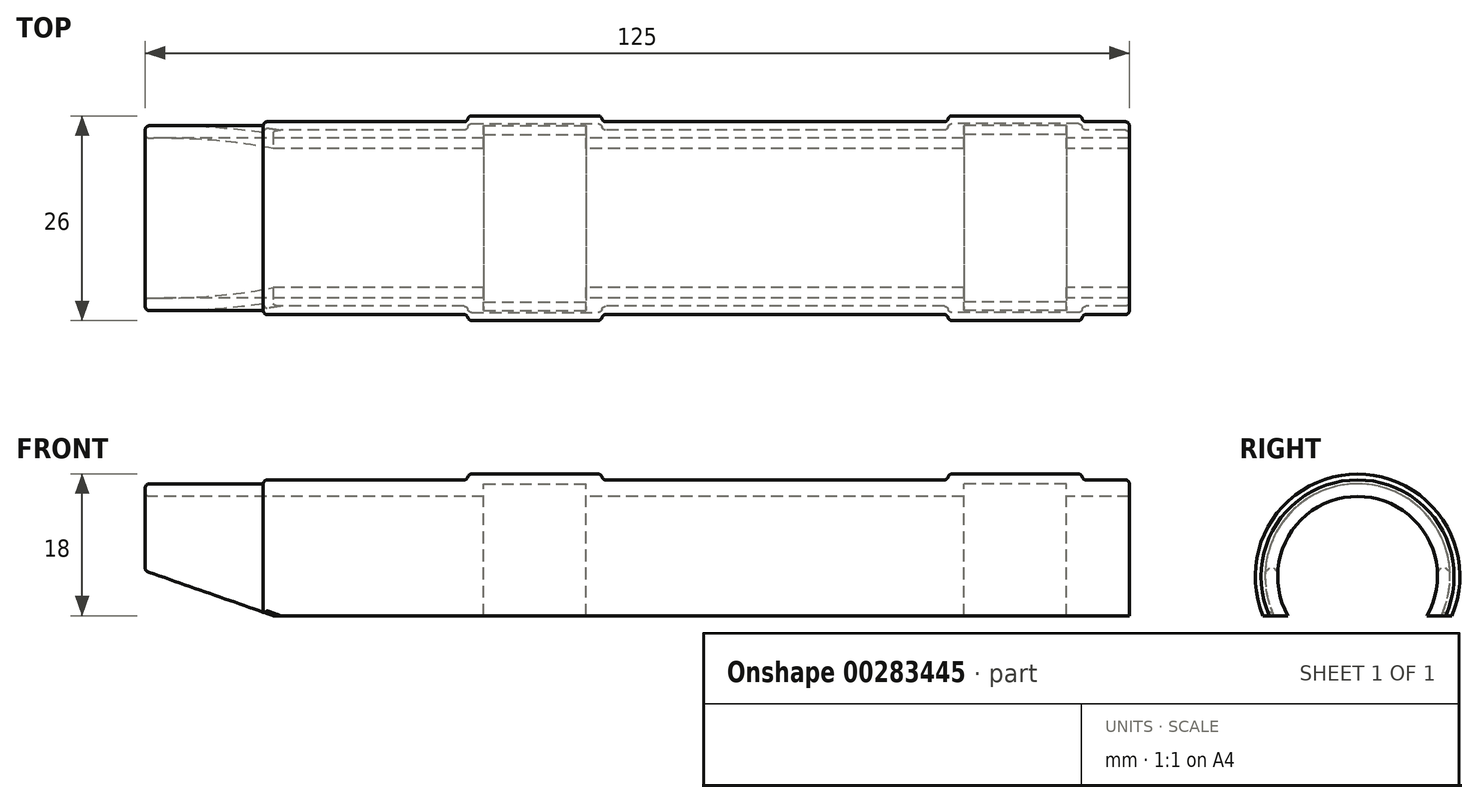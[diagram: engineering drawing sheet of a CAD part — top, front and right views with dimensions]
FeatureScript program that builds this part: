
annotation { "Feature Type Name" : "Feature", "Feature Type Description" : "" }
export const myFeature = defineFeature(function(context is Context, id is Id, definition is map)
    precondition{}
    {
        {
            var Q0;
            Q0=qCreatedBy(makeId("Right.planeOp"),FACE);
            var sketch = newSketch(context, id + "F0", { "sketchPlane" : qUnion([Q0])});
            skCircle(sketch, "E0", {"center": v(0, 0) * mm, "radius": 10.15 * mm});
            skCircle(sketch, "E1", {"center": v(0, 0) * mm, "radius": 11.75 * mm});
            skCircle(sketch, "E2", {"center": v(0, 0) * mm, "radius": 12.25 * mm});
            skLineSegment(sketch, "E3", {"start": v(0, 0) * mm, "end": v(15.86, -16.54) * mm});
            skLineSegment(sketch, "E4", {"start": v(0, 0) * mm, "end": v(-17.88, -17.15) * mm});
            skCircle(sketch, "E5", {"center": v(0, 0) * mm, "radius": 13 * mm});
            skSolve(sketch);
        }
        {
            var Q0;
            {var subQ0=sQuery(id+"F0.wireOp",EDGE,"E3");var subQ1=sQuery(id+"F0.wireOp",EDGE,"E0");var subQ2=makeQuery(id+"F0.imprint","INTERSECT",VERTEX,{"derivedFrom":[subQ1,subQ0]});Q0=makeQuery(id+"F0.imprint","IMPRINT",FACE,{"disambiguationData":[TD([[makeQuery(id+"F0.imprint","IMPRINT",EDGE,{"disambiguationData":[TD([[subQ2,-1.0]])],"derivedFrom":subQ1}),-1.0]])]});}
            extrude(context, id + "F1", {"entities" : qUnion([Q0]), "depth" : 55 * mm, "hasSecondDirection" : true, "secondDirectionOppositeDirection" : true, "secondDirectionDepth" : 70 * mm});
        }
        {
            var Q0;
            {var subQ0=sQuery(id+"F0.wireOp",EDGE,"E3");var subQ1=sQuery(id+"F0.wireOp",EDGE,"E1");var subQ2=makeQuery(id+"F0.imprint","INTERSECT",VERTEX,{"derivedFrom":[subQ1,subQ0]});Q0=makeQuery(id+"F0.imprint","IMPRINT",FACE,{"disambiguationData":[TD([[makeQuery(id+"F0.imprint","IMPRINT",EDGE,{"disambiguationData":[TD([[subQ2,-1.0]])],"derivedFrom":subQ1}),-1.0]])]});}
            extrude(context, id + "F2", {"entities" : qUnion([Q0]), "operationType" : NewBodyOperationType.ADD, "depth" : 110 * mm, "symmetric" : true});
        }
        {
            var Q0;
            {var subQ0=sQuery(id+"F0.wireOp",EDGE,"E3");var subQ1=sQuery(id+"F0.wireOp",EDGE,"E2");var subQ2=makeQuery(id+"F0.imprint","INTERSECT",VERTEX,{"derivedFrom":[subQ1,subQ0]});Q0=makeQuery(id+"F0.imprint","IMPRINT",FACE,{"disambiguationData":[TD([[makeQuery(id+"F0.imprint","IMPRINT",EDGE,{"disambiguationData":[TD([[subQ2,-1.0]])],"derivedFrom":subQ1}),-1.0]])]});}
            extrude(context, id + "F3", {"entities" : qUnion([Q0]), "operationType" : NewBodyOperationType.ADD, "depth" : 49 * mm, "hasSecondDirection" : true, "secondDirectionOppositeDirection" : false, "secondDirectionDepth" : 32 * mm});
        }
        {
            var Q0;
            {var subQ0=sQuery(id+"F0.wireOp",EDGE,"E3");var subQ1=sQuery(id+"F0.wireOp",EDGE,"E2");var subQ2=makeQuery(id+"F0.imprint","INTERSECT",VERTEX,{"derivedFrom":[subQ1,subQ0]});Q0=makeQuery(id+"F0.imprint","IMPRINT",FACE,{"disambiguationData":[TD([[makeQuery(id+"F0.imprint","IMPRINT",EDGE,{"disambiguationData":[TD([[subQ2,-1.0]])],"derivedFrom":subQ1}),-1.0]])]});}
            extrude(context, id + "F4", {"entities" : qUnion([Q0]), "operationType" : NewBodyOperationType.ADD, "oppositeDirection" : true, "depth" : 29 * mm, "hasSecondDirection" : true, "secondDirectionOppositeDirection" : true, "secondDirectionDepth" : 12 * mm});
        }
        {
            var Q0;
            {var subQ0=sQuery(id+"F0.wireOp",EDGE,"E3");var subQ1=sQuery(id+"F0.wireOp",EDGE,"E0");var subQ2=makeQuery(id+"F0.imprint","INTERSECT",VERTEX,{"derivedFrom":[subQ1,subQ0]});Q0=makeQuery(id+"F0.imprint","IMPRINT",FACE,{"disambiguationData":[TD([[makeQuery(id+"F0.imprint","IMPRINT",EDGE,{"disambiguationData":[TD([[subQ2,-1.0]])],"derivedFrom":subQ1}),-1.0]])]});}
            extrude(context, id + "F5", {"entities" : qUnion([Q0]), "operationType" : NewBodyOperationType.REMOVE, "depth" : 47 * mm, "hasSecondDirection" : true, "secondDirectionOppositeDirection" : false, "secondDirectionDepth" : 34 * mm});
        }
        {
            var Q0;
            {var subQ0=sQuery(id+"F0.wireOp",EDGE,"E3");var subQ1=sQuery(id+"F0.wireOp",EDGE,"E0");var subQ2=makeQuery(id+"F0.imprint","INTERSECT",VERTEX,{"derivedFrom":[subQ1,subQ0]});Q0=makeQuery(id+"F0.imprint","IMPRINT",FACE,{"disambiguationData":[TD([[makeQuery(id+"F0.imprint","IMPRINT",EDGE,{"disambiguationData":[TD([[subQ2,-1.0]])],"derivedFrom":subQ1}),-1.0]])]});}
            extrude(context, id + "F6", {"entities" : qUnion([Q0]), "operationType" : NewBodyOperationType.REMOVE, "oppositeDirection" : true, "depth" : 27 * mm, "hasSecondDirection" : true, "secondDirectionOppositeDirection" : true, "secondDirectionDepth" : 14 * mm});
        }
        {
            var Q0;
            Q0=qCreatedBy(makeId("Front.planeOp"),FACE);
            var sketch = newSketch(context, id + "F7", { "sketchPlane" : qUnion([Q0])});
            skLineSegment(sketch, "E6", {"start": v(-38.6, -10.28) * mm, "end": v(-89.03, 7.33) * mm});
            skLineSegment(sketch, "E7", {"start": v(-89.03, 7.33) * mm, "end": v(-89.03, -10.28) * mm});
            skLineSegment(sketch, "E8", {"start": v(-89.03, -10.28) * mm, "end": v(-38.6, -10.28) * mm});
            skSolve(sketch);
        }
        {
            var Q0;
            Q0=makeQuery(id+"F7.imprint","IMPRINT",FACE,{"disambiguationData":[TD([[makeQuery(id+"F7.imprint","IMPRINT",EDGE,{"derivedFrom":sQuery(id+"F7.wireOp",EDGE,"E6")}),1.0]])]});
            extrude(context, id + "F8", {"entities" : qUnion([Q0]), "operationType" : NewBodyOperationType.REMOVE, "oppositeDirection" : true, "depth" : 25 * mm, "symmetric" : true});
        }
        {
            var Q0;
            {var subQ0=sQuery(id+"F0.wireOp",EDGE,"E4");var subQ1=sQuery(id+"F0.wireOp",EDGE,"E3");var subQ2=sQuery(id+"F0.wireOp",EDGE,"E2");var subQ3=sQuery(id+"F0.wireOp",EDGE,"E1");Q0=makeQuery(id+"F3.boolean.opBoolean","SPLIT",FACE,{"disambiguationData":[TD([makeQuery(id+"F1.opExtrude","CAP_FACE",FACE,{"disambiguationData":[OSD([sQuery(id+"F0.wireOp",EDGE,"E0"),subQ3,subQ1,subQ0])],"isStart":false})])],"derivedFrom":makeQuery(id+"F2.opExtrude","SWEPT_FACE",FACE,{"disambiguationData":[OSD([subQ2])]})});}
            var Q1;
            {var subQ0=sQuery(id+"F0.wireOp",EDGE,"E4");var subQ2=sQuery(id+"F0.wireOp",EDGE,"E3");var subQ7=sQuery(id+"F0.wireOp",EDGE,"E5");var subQ8=sQuery(id+"F0.wireOp",EDGE,"E2");var subQ9=makeQuery(id+"F3.opExtrude","CAP_FACE",FACE,{"disambiguationData":[OSD([subQ8,subQ2,subQ0,subQ7])],"isStart":true});Q1=makeQuery(id+"F4.boolean.opBoolean","SPLIT",FACE,{"disambiguationData":[TD([subQ9])],"derivedFrom":makeQuery(id+"F3.boolean.opBoolean","SPLIT",FACE,{"disambiguationData":[TD([makeQuery(id+"F2.opExtrude","CAP_FACE",FACE,{"disambiguationData":[OSD([sQuery(id+"F0.wireOp",EDGE,"E1"),subQ8,subQ2,subQ0])],"isStart":true})])],"derivedFrom":makeQuery(id+"F2.opExtrude","SWEPT_FACE",FACE,{"disambiguationData":[OSD([subQ8])]})})});}
            var Q2;
            {var subQ0=sQuery(id+"F0.wireOp",EDGE,"E3");var subQ3=sQuery(id+"F0.wireOp",EDGE,"E4");var subQ4=sQuery(id+"F0.wireOp",EDGE,"E2");var subQ5=makeQuery(id+"F2.opExtrude","CAP_FACE",FACE,{"disambiguationData":[OSD([sQuery(id+"F0.wireOp",EDGE,"E1"),subQ4,subQ0,subQ3])],"isStart":true});Q2=makeQuery(id+"F4.boolean.opBoolean","SPLIT",FACE,{"disambiguationData":[TD([subQ5])],"derivedFrom":makeQuery(id+"F3.boolean.opBoolean","SPLIT",FACE,{"disambiguationData":[TD([subQ5])],"derivedFrom":makeQuery(id+"F2.opExtrude","SWEPT_FACE",FACE,{"disambiguationData":[OSD([subQ4])]})})});}
            fillet(context, id + "F9", {"entities" : qUnion([Q0, Q1, Q2]), "radius" : .5 * mm, "allowEdgeOverflow" : false});
        }
        {
            var Q0;
            Q0=makeQuery(id+"F3.opExtrude","SWEPT_FACE",FACE,{"disambiguationData":[OSD([sQuery(id+"F0.wireOp",EDGE,"E5")])]});
            var Q1;
            Q1=makeQuery(id+"F4.opExtrude","SWEPT_FACE",FACE,{"disambiguationData":[OSD([sQuery(id+"F0.wireOp",EDGE,"E5")])]});
            fillet(context, id + "F10", {"entities" : qUnion([Q0, Q1]), "radius" : .5 * mm, "tangentPropagation" : true, "allowEdgeOverflow" : false});
        }
        {
            var Q0;
            Q0=makeQuery(id+"F1.opExtrude","CAP_FACE",FACE,{"disambiguationData":[OSD([sQuery(id+"F0.wireOp",EDGE,"E0"),sQuery(id+"F0.wireOp",EDGE,"E1"),sQuery(id+"F0.wireOp",EDGE,"E3"),sQuery(id+"F0.wireOp",EDGE,"E4")])],"isStart":true});
            fillet(context, id + "F11", {"entities" : qUnion([Q0]), "radius" : .5 * mm, "tangentPropagation" : true, "allowEdgeOverflow" : false});
        }
        {
            var Q0;
            Q0=qCreatedBy(makeId("Front.planeOp"),FACE);
            var sketch = newSketch(context, id + "F12", { "sketchPlane" : qUnion([Q0])});
            skLineSegment(sketch, "E9", {"start": v(74.89, -5) * mm, "end": v(-86.34, -5) * mm});
            skLineSegment(sketch, "E10", {"start": v(-86.34, -5) * mm, "end": v(-86.34, -15.33) * mm});
            skLineSegment(sketch, "E11", {"start": v(-86.34, -15.33) * mm, "end": v(74.89, -15.33) * mm});
            skLineSegment(sketch, "E12", {"start": v(74.89, -15.33) * mm, "end": v(74.89, -5) * mm});
            skSolve(sketch);
        }
        {
            var Q0;
            Q0=makeQuery(id+"F12.imprint","IMPRINT",FACE,{"disambiguationData":[TD([[makeQuery(id+"F12.imprint","IMPRINT",EDGE,{"derivedFrom":sQuery(id+"F12.wireOp",EDGE,"E9")}),1.0]])]});
            extrude(context, id + "F13", {"entities" : qUnion([Q0]), "operationType" : NewBodyOperationType.REMOVE, "oppositeDirection" : true, "depth" : 47.6 * mm, "symmetric" : true});
        }
    });
